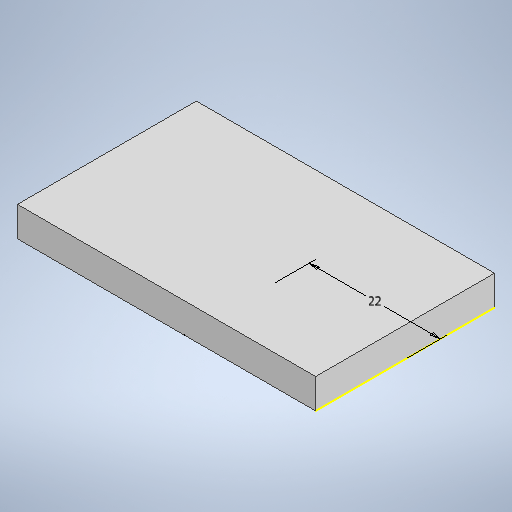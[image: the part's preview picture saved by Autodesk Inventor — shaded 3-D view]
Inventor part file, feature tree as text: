
AUTODESK INVENTOR PART (.ipt)
format: ipt  version: 2025.1 (Build 291241020, 241B)  size: 213,504 bytes
history: native  units: in
note: dims shown in document units (in); Inventor stores cm internally (conversion verified against a paired STEP export)
features: sketch x2, extrude x1
ambient origin geometry x8: Origin, YZ Plane, XZ Plane, XY Plane, X Axis, Y Axis, Z Axis, Center Point
bodies: Solid1 (feature_tree)
feature tree (3):
  extrude  "Extrusion1"  Depth=1.1811in
  sketch  "Sketch2"  dims[d2=0.1969in d3=0.0in d4=0.8661in d5=0.0344in]
  sketch  "Sketch1"  dims[d0=1.9685in d1=1.1811in]
